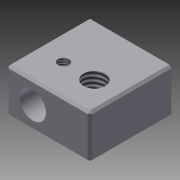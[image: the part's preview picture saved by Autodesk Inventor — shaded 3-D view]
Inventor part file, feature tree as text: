
AUTODESK INVENTOR PART (.ipt)
format: ipt  version: 2015 (Build 190159000, 159)  size: 138,752 bytes
history: native  units: mm
features: hole x4, extrude x1, chamfer x1
ambient origin geometry x8: Origin, YZ Plane, XZ Plane, XY Plane, X Axis, Y Axis, Z Axis, Center Point
bodies: Solid1 (feature_tree)
feature tree (6):
  extrude  "Extrusión1"  Depth=19.0mm
  hole  "Agujero1"  [1 undecoded]
  hole  "Agujero2"  [1 undecoded]
  hole  "Agujero3"  [1 undecoded]
  hole  "Agujero4"  [1 undecoded]
  chamfer  "Chaflán1"  Distance=0.5mm Angle=45.0deg
note: 4 required parameter values undecoded (feature->parameter linkage not recoverable at this tier; creation-order binding heuristic only, values carry confidence <= 0.55)
